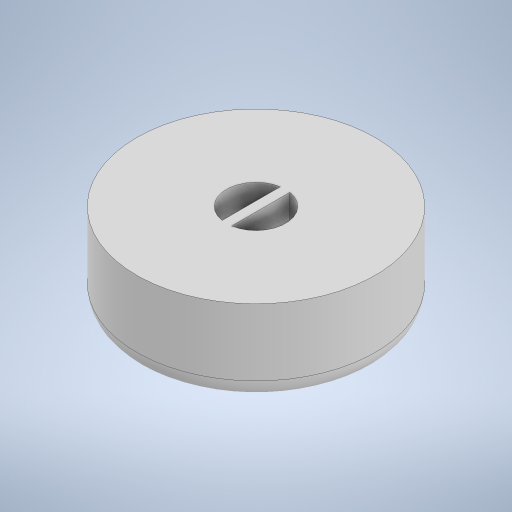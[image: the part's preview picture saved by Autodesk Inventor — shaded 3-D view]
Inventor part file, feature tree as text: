
AUTODESK INVENTOR PART (.ipt)
format: ipt  version: 2023 (Build 270158000, 158)  size: 232,448 bytes
history: native  units: in
note: dims shown in document units (in); Inventor stores cm internally (conversion verified against a paired STEP export)
features: extrude x3, sketch x1, fillet x1
ambient origin geometry x8: Origin, YZ Plane, XZ Plane, XY Plane, X Axis, Y Axis, Z Axis, Center Point
bodies: Solid1 (feature_tree)
feature tree (5):
  sketch  "Sketch1"  dims[d0=0.2441in d1=0.9843in d3=0.0394in d4=0.2756in d5=0.0in d6=0.2756in d7=0.0in d8=0.0787in d9=0.0in d10=0.0787in]
  extrude  "Extrusion1"  Depth=0.0787in
  extrude  "Extrusion2"  Depth=0.0394in
  extrude  "Extrusion3"  Depth=0.2756in TaperAngle=0.0deg
  fillet  "Fillet1"  Radius=0.2756in
